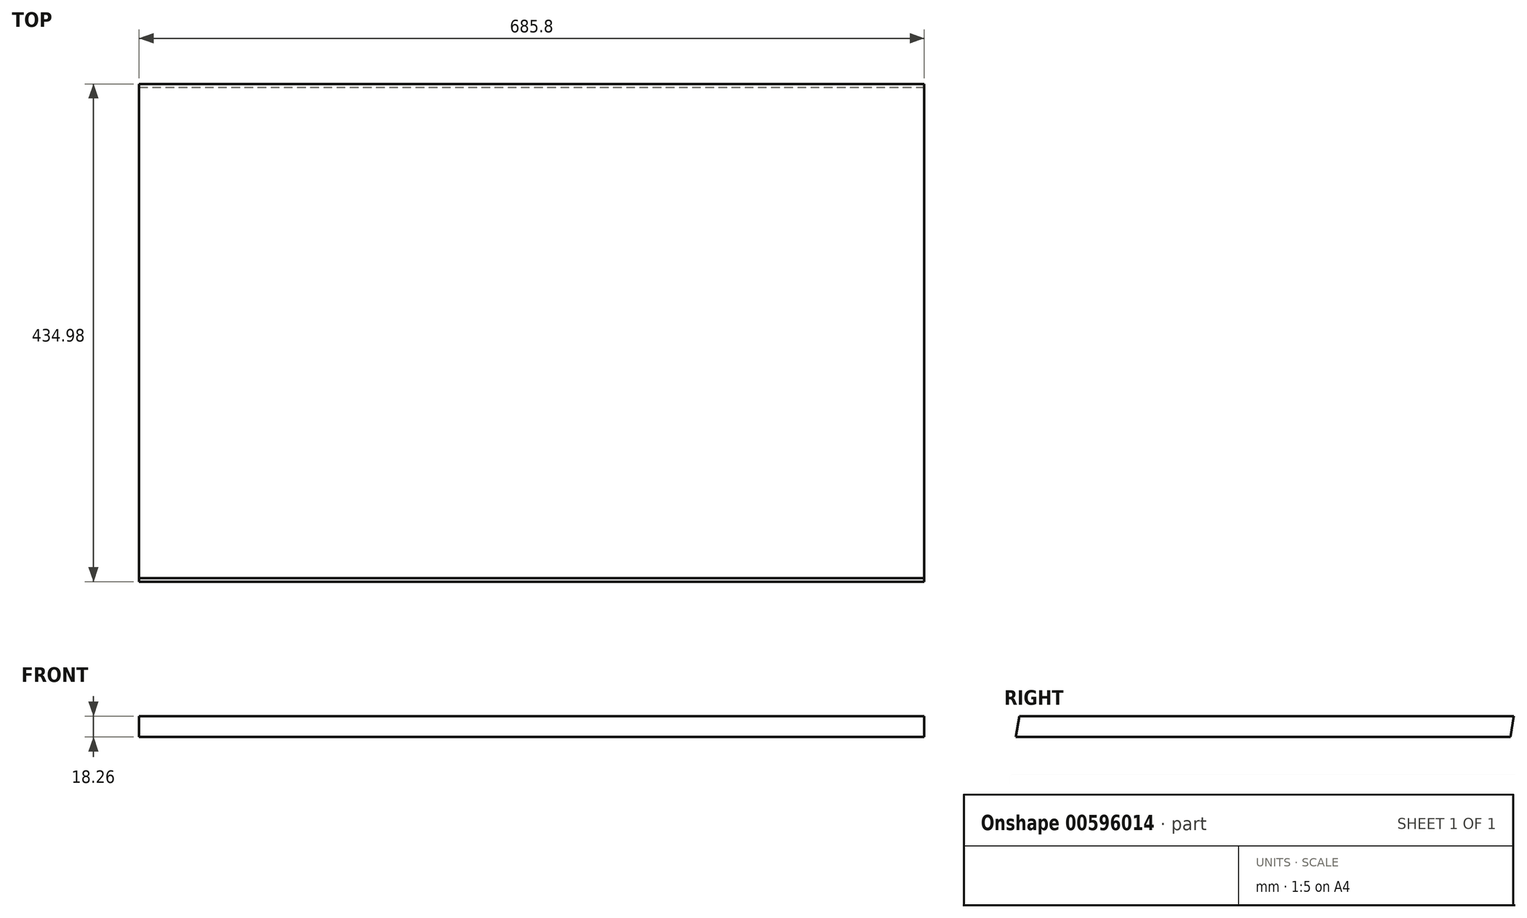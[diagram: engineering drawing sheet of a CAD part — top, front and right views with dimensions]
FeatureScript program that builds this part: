
annotation { "Feature Type Name" : "Feature", "Feature Type Description" : "" }
export const myFeature = defineFeature(function(context is Context, id is Id, definition is map)
    precondition{}
    {
        {
            var Q0;
            Q0=qCreatedBy(makeId("Right.planeOp"),FACE);
            var sketch = newSketch(context, id + "F0", { "sketchPlane" : qUnion([Q0])});
            skLineSegment(sketch, "E0.bottom", {"start": v(217.49, 9.13) * mm, "end": v(-217.49, 9.13) * mm});
            skLineSegment(sketch, "E0.top", {"start": v(217.49, -9.13) * mm, "end": v(-217.49, -9.13) * mm});
            skLineSegment(sketch, "E0.left", {"start": v(217.49, 9.13) * mm, "end": v(217.49, -9.13) * mm});
            skLineSegment(sketch, "E0.right", {"start": v(-217.49, 9.13) * mm, "end": v(-217.49, -9.13) * mm});
            skPoint(sketch, "E0.middle", {"position": v(0, 0) * mm});
            skSolve(sketch);
        }
        {
            var Q0;
            Q0 = qSketchRegion(id + "F0", true);
            extrude(context, id + "F1", {"entities" : qUnion([Q0]), "endBound" : BoundingType.SYMMETRIC, "depth" : 685.8 * mm, "offsetDistance" : 25.4 * mm});
        }
        {
            var Q0;
            Q0=makeQuery(id+"F1.opExtrude","CAP_FACE",FACE,{"disambiguationData":[OSD([sQuery(id+"F0.wireOp",EDGE,"E0.bottom"),sQuery(id+"F0.wireOp",EDGE,"E0.top"),sQuery(id+"F0.wireOp",EDGE,"E0.left"),sQuery(id+"F0.wireOp",EDGE,"E0.right")])],"isStart":false});
            var sketch = newSketch(context, id + "F2", { "sketchPlane" : qUnion([Q0])});
            skLineSegment(sketch, "E1", {"start": v(217.49, 9.13) * mm, "end": v(214.5, -9.13) * mm});
            skLineSegment(sketch, "E2", {"start": v(214.5, -9.13) * mm, "end": v(217.49, -9.13) * mm});
            skLineSegment(sketch, "E3", {"start": v(217.49, -9.13) * mm, "end": v(217.49, 9.13) * mm});
            skLineSegment(sketch, "E4", {"start": v(-217.49, 9.13) * mm, "end": v(-214.5, 9.13) * mm});
            skLineSegment(sketch, "E5", {"start": v(-214.5, 9.13) * mm, "end": v(-217.49, -9.13) * mm});
            skLineSegment(sketch, "E6", {"start": v(-217.49, -9.13) * mm, "end": v(-217.49, 9.13) * mm});
            skSolve(sketch);
        }
        {
            var Q0;
            Q0 = qSketchRegion(id + "F2", true);
            extrude(context, id + "F3", {"entities" : qUnion([Q0]), "operationType" : NewBodyOperationType.REMOVE, "endBound" : BoundingType.UP_TO_NEXT, "oppositeDirection" : true, "depth" : 25.4 * mm, "offsetDistance" : 25.4 * mm});
        }
    });
